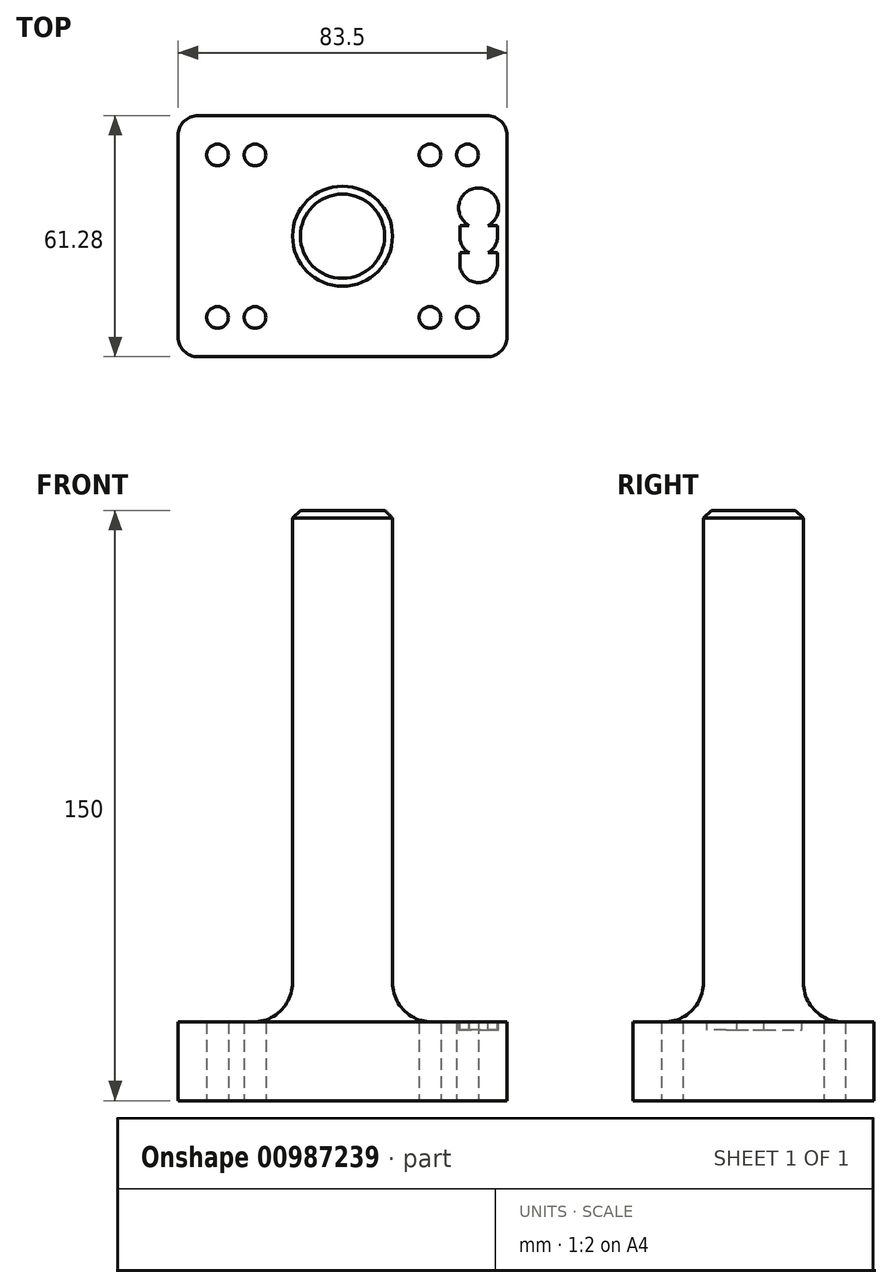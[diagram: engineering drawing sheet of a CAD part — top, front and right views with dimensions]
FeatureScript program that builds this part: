
annotation { "Feature Type Name" : "Feature", "Feature Type Description" : "" }
export const myFeature = defineFeature(function(context is Context, id is Id, definition is map)
    precondition{}
    {
        {
            var Q0;
            Q0=qCreatedBy(makeId("Top.planeOp"),FACE);
            var sketch = newSketch(context, id + "F0", { "sketchPlane" : qUnion([Q0])});
            skLineSegment(sketch, "E0.bottom", {"start": v(-41.75, 30.64) * mm, "end": v(41.75, 30.64) * mm});
            skLineSegment(sketch, "E0.top", {"start": v(-41.75, -30.64) * mm, "end": v(41.75, -30.64) * mm});
            skLineSegment(sketch, "E0.left", {"start": v(-41.75, 30.64) * mm, "end": v(-41.75, -30.64) * mm});
            skLineSegment(sketch, "E0.right", {"start": v(41.75, 30.64) * mm, "end": v(41.75, -30.64) * mm});
            skPoint(sketch, "E0.middle", {"position": v(0, 0) * mm});
            skCircle(sketch, "E1", {"center": v(-31.75, 20.64) * mm, "radius": 2.75 * mm});
            skCircle(sketch, "E2", {"center": v(-22.23, 20.64) * mm, "radius": 2.75 * mm});
            skCircle(sketch, "E3", {"center": v(-31.75, -20.64) * mm, "radius": 2.75 * mm});
            skCircle(sketch, "E4", {"center": v(-22.23, -20.64) * mm, "radius": 2.75 * mm});
            skCircle(sketch, "E5", {"center": v(22.23, 20.64) * mm, "radius": 2.75 * mm});
            skCircle(sketch, "E6", {"center": v(31.75, 20.64) * mm, "radius": 2.75 * mm});
            skCircle(sketch, "E7", {"center": v(22.23, -20.64) * mm, "radius": 2.75 * mm});
            skCircle(sketch, "E8", {"center": v(31.75, -20.64) * mm, "radius": 2.75 * mm});
            skSolve(sketch);
        }
        {
            var Q0;
            Q0 = qSketchRegion(id + "F0", true);
            extrude(context, id + "F1", {"entities" : qUnion([Q0]), "depth" : 20 * mm, "offsetDistance" : 25 * mm});
        }
        {
            var Q0;
            Q0=makeQuery(id+"F1.opExtrude","SWEPT_EDGE",EDGE,{"disambiguationData":[OSD([sQuery(id+"F0.wireOp",EDGE,"E0.top"),sQuery(id+"F0.wireOp",EDGE,"E0.left")])]});
            var Q1;
            Q1=makeQuery(id+"F1.opExtrude","SWEPT_EDGE",EDGE,{"disambiguationData":[OSD([sQuery(id+"F0.wireOp",EDGE,"E0.top"),sQuery(id+"F0.wireOp",EDGE,"E0.right")])]});
            var Q2;
            Q2=makeQuery(id+"F1.opExtrude","SWEPT_EDGE",EDGE,{"disambiguationData":[OSD([sQuery(id+"F0.wireOp",EDGE,"E0.bottom"),sQuery(id+"F0.wireOp",EDGE,"E0.left")])]});
            var Q3;
            Q3=makeQuery(id+"F1.opExtrude","SWEPT_EDGE",EDGE,{"disambiguationData":[OSD([sQuery(id+"F0.wireOp",EDGE,"E0.bottom"),sQuery(id+"F0.wireOp",EDGE,"E0.right")])]});
            fillet(context, id + "F2", {"entities" : qUnion([Q0, Q1, Q2, Q3]), "radius" : 5 * mm, "tangentPropagation" : true, "allowEdgeOverflow" : false});
        }
        {
            var Q0;
            Q0=qCreatedBy(makeId("Top.planeOp"),FACE);
            var sketch = newSketch(context, id + "F3", { "sketchPlane" : qUnion([Q0])});
            skCircle(sketch, "E9", {"center": v(0, 0) * mm, "radius": 12.7 * mm});
            skSolve(sketch);
        }
        {
            var Q0;
            Q0 = qSketchRegion(id + "F3", true);
            extrude(context, id + "F4", {"entities" : qUnion([Q0]), "operationType" : NewBodyOperationType.ADD, "depth" : 150 * mm, "offsetDistance" : 25 * mm});
        }
        {
            var Q0;
            Q0=makeQuery(id+"F4.opExtrude","CAP_EDGE",EDGE,{"disambiguationData":[OSD([sQuery(id+"F3.wireOp",EDGE,"E9")])],"isStart":false});
            chamfer(context, id + "F5", {"entities" : qUnion([Q0]), "width" : 2 * mm, "tangentPropagation" : true});
        }
        {
            var Q0;
            Q0=makeQuery(id+"F4.boolean.opBoolean","INTERSECT",EDGE,{"derivedFrom":[makeQuery(id+"F1.opExtrude","CAP_FACE",FACE,{"disambiguationData":[OSD([sQuery(id+"F0.wireOp",EDGE,"E0.bottom"),sQuery(id+"F0.wireOp",EDGE,"E0.top"),sQuery(id+"F0.wireOp",EDGE,"E0.left"),sQuery(id+"F0.wireOp",EDGE,"E0.right"),sQuery(id+"F0.wireOp",EDGE,"E1"),sQuery(id+"F0.wireOp",EDGE,"E2"),sQuery(id+"F0.wireOp",EDGE,"E3"),sQuery(id+"F0.wireOp",EDGE,"E4"),sQuery(id+"F0.wireOp",EDGE,"E5"),sQuery(id+"F0.wireOp",EDGE,"E6"),sQuery(id+"F0.wireOp",EDGE,"E7"),sQuery(id+"F0.wireOp",EDGE,"E8")])],"isStart":false}),makeQuery(id+"F4.opExtrude","SWEPT_FACE",FACE,{"disambiguationData":[OSD([sQuery(id+"F3.wireOp",EDGE,"E9")])]})]});
            fillet(context, id + "F6", {"entities" : qUnion([Q0]), "radius" : 10 * mm, "tangentPropagation" : true, "defaultsChanged" : true, "vertexSettings" : [], "allowEdgeOverflow" : false});
        }
        {
            var Q0;
            Q0=makeQuery(id+"F1.opExtrude","CAP_FACE",FACE,{"disambiguationData":[OSD([sQuery(id+"F0.wireOp",EDGE,"E0.bottom"),sQuery(id+"F0.wireOp",EDGE,"E0.top"),sQuery(id+"F0.wireOp",EDGE,"E0.left"),sQuery(id+"F0.wireOp",EDGE,"E0.right"),sQuery(id+"F0.wireOp",EDGE,"E1"),sQuery(id+"F0.wireOp",EDGE,"E2"),sQuery(id+"F0.wireOp",EDGE,"E3"),sQuery(id+"F0.wireOp",EDGE,"E4"),sQuery(id+"F0.wireOp",EDGE,"E5"),sQuery(id+"F0.wireOp",EDGE,"E6"),sQuery(id+"F0.wireOp",EDGE,"E7"),sQuery(id+"F0.wireOp",EDGE,"E8")])],"isStart":false});
            var sketch = newSketch(context, id + "F7", { "sketchPlane" : qUnion([Q0])});
            skArc(sketch, "E10", {"start": v(29.8, -0.07) * mm, "mid": v(30.44, -2.47) * mm, "end": v(32.2, -4.22) * mm});
            skLineSegment(sketch, "E11.top", {"start": v(39.36, 2.73) * mm, "end": v(36.99, 2.73) * mm});
            skLineSegment(sketch, "E11.left", {"start": v(39.36, -0.07) * mm, "end": v(39.36, 2.73) * mm});
            skLineSegment(sketch, "E11.right", {"start": v(29.8, -0.07) * mm, "end": v(29.8, 2.73) * mm});
            skArc(sketch, "E12", {"start": v(29.8, -7.02) * mm, "mid": v(34.58, -11.8) * mm, "end": v(39.36, -7.02) * mm});
            skLineSegment(sketch, "E13.top", {"start": v(39.36, -4.22) * mm, "end": v(36.96, -4.22) * mm});
            skLineSegment(sketch, "E13.left", {"start": v(39.36, -7.02) * mm, "end": v(39.36, -4.22) * mm});
            skLineSegment(sketch, "E13.right", {"start": v(29.8, -7.02) * mm, "end": v(29.8, -4.22) * mm});
            skLineSegment(sketch, "E14.trimOffspring", {"start": v(32.2, -4.22) * mm, "end": v(29.8, -4.22) * mm});
            skArc(sketch, "E15.trimOffspring", {"start": v(36.96, -4.22) * mm, "mid": v(38.72, -2.47) * mm, "end": v(39.36, -0.07) * mm});
            skArc(sketch, "E16", {"start": v(36.99, 2.73) * mm, "mid": v(34.58, 12.28) * mm, "end": v(32.17, 2.73) * mm});
            skLineSegment(sketch, "E17.trimOffspring", {"start": v(32.17, 2.73) * mm, "end": v(29.8, 2.73) * mm});
            skSolve(sketch);
        }
        {
            var Q0;
            Q0 = qSketchRegion(id + "F7", true);
            extrude(context, id + "F8", {"entities" : qUnion([Q0]), "operationType" : NewBodyOperationType.REMOVE, "oppositeDirection" : true, "depth" : 2 * mm, "offsetDistance" : 25 * mm});
        }
    });
